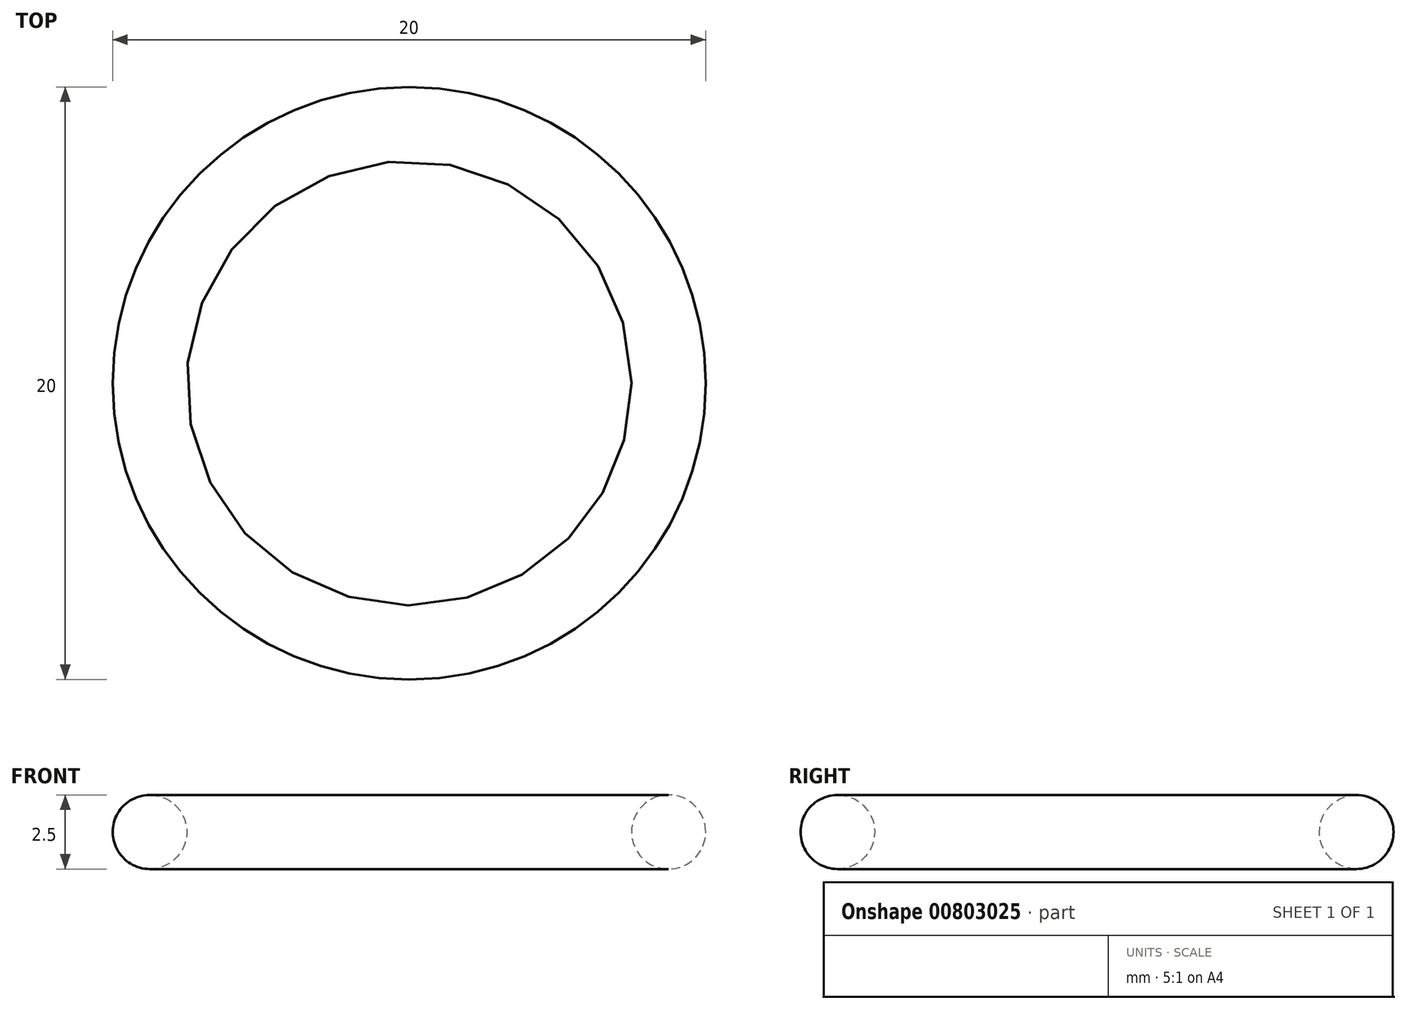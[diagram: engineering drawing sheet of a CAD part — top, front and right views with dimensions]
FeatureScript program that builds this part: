
annotation { "Feature Type Name" : "Feature", "Feature Type Description" : "" }
export const myFeature = defineFeature(function(context is Context, id is Id, definition is map)
    precondition{}
    {
        {
            var Q0;
            Q0=qCreatedBy(makeId("Front.planeOp"),FACE);
            var sketch = newSketch(context, id + "F0", { "sketchPlane" : qUnion([Q0])});
            skCircle(sketch, "E0", {"center": v(-8.75, 0) * mm, "radius": 1.25 * mm});
            skLineSegment(sketch, "E1", {"start": v(0, 9.43) * mm, "end": v(0, -8.34) * mm, "construction": true});
            skSolve(sketch);
        }
        {
            var Q0;
            Q0 = qSketchRegion(id + "F0", true);
            var Q1;
            Q1=sQuery(id+"F0.wireOp",EDGE,"E1");
            revolve(context, id + "F1", {"surfaceOperationType" : NewSurfaceOperationType.NEW, "entities" : qUnion([Q0]), "axis" : qUnion([Q1]), "revolveType" : RevolveType.FULL});
        }
    });
